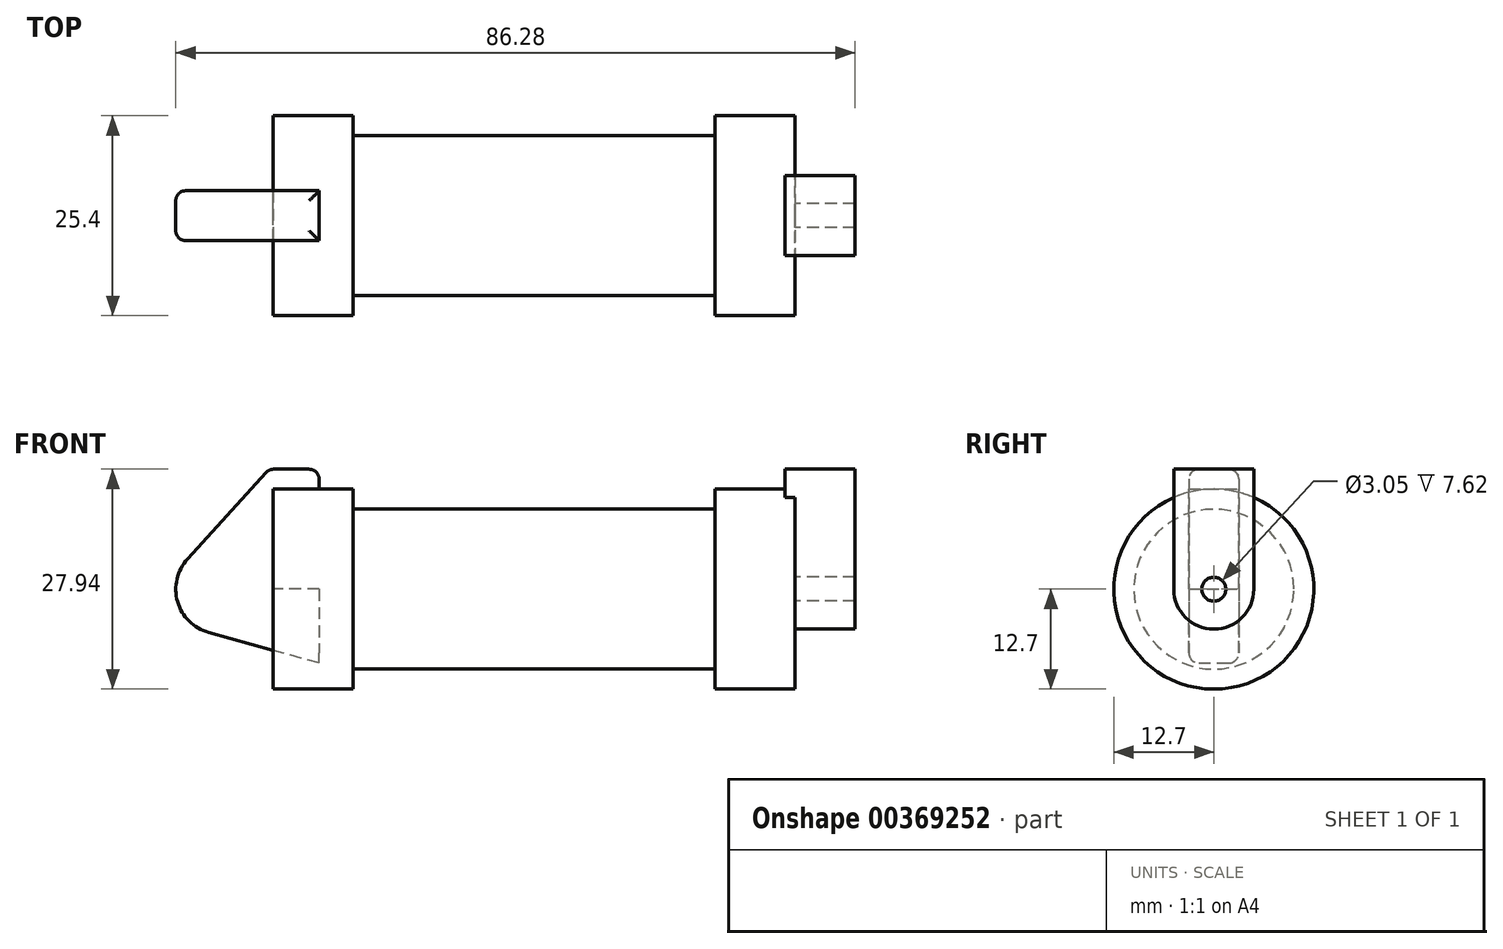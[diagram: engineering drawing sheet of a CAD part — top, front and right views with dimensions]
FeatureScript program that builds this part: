
annotation { "Feature Type Name" : "Feature", "Feature Type Description" : "" }
export const myFeature = defineFeature(function(context is Context, id is Id, definition is map)
    precondition{}
    {
        {
            var Q0;
            Q0=qCreatedBy(makeId("Front.planeOp"),FACE);
            var sketch = newSketch(context, id + "F0", { "sketchPlane" : qUnion([Q0])});
            skLineSegment(sketch, "E0", {"start": v(0, 0) * mm, "end": v(0, 12.7) * mm});
            skLineSegment(sketch, "E1", {"start": v(0, 12.7) * mm, "end": v(10.16, 12.7) * mm});
            skLineSegment(sketch, "E2", {"start": v(10.16, 12.7) * mm, "end": v(10.16, 10.16) * mm});
            skLineSegment(sketch, "E3", {"start": v(10.16, 10.16) * mm, "end": v(56.13, 10.16) * mm});
            skLineSegment(sketch, "E4", {"start": v(56.13, 10.16) * mm, "end": v(56.13, 12.7) * mm});
            skLineSegment(sketch, "E5", {"start": v(56.13, 12.7) * mm, "end": v(66.3, 12.7) * mm});
            skLineSegment(sketch, "E6", {"start": v(66.3, 12.7) * mm, "end": v(66.3, 0) * mm});
            skLineSegment(sketch, "E7", {"start": v(66.3, 0) * mm, "end": v(0, 0) * mm});
            skLineSegment(sketch, "E8", {"start": v(5.84, 15.24) * mm, "end": v(-0.5, 15.24) * mm});
            skLineSegment(sketch, "E9", {"start": v(-0.5, 15.24) * mm, "end": v(-10.88, 3.85) * mm});
            skLineSegment(sketch, "E10", {"start": v(0, 0) * mm, "end": v(-6.65, 0) * mm});
            skCircle(sketch, "E11", {"center": v(-6.65, 0) * mm, "radius": 5.72 * mm});
            skCircle(sketch, "E12", {"center": v(-6.65, 0) * mm, "radius": 3.18 * mm});
            skLineSegment(sketch, "E13", {"start": v(5.84, 15.24) * mm, "end": v(5.84, -9.4) * mm});
            skLineSegment(sketch, "E14", {"start": v(5.84, -9.4) * mm, "end": v(-8.18, -5.5) * mm});
            skSolve(sketch);
        }
        {
            var Q0;
            {var subQ0=sQuery(id+"F0.wireOp",EDGE,"E0");Q0=makeQuery(id+"F0.imprint","IMPRINT",FACE,{"disambiguationData":[TD([[makeQuery(id+"F0.imprint","IMPRINT",EDGE,{"derivedFrom":subQ0}),-1.0]])]});}
            var Q1;
            {var subQ0=sQuery(id+"F0.wireOp",EDGE,"E2");Q1=makeQuery(id+"F0.imprint","IMPRINT",FACE,{"disambiguationData":[TD([[makeQuery(id+"F0.imprint","IMPRINT",EDGE,{"derivedFrom":subQ0}),-1.0]])]});}
            var Q2;
            Q2=sQuery(id+"F0.wireOp",EDGE,"E7");
            revolve(context, id + "F1", {"entities" : qUnion([Q0, Q1]), "axis" : qUnion([Q2]), "revolveType" : RevolveType.FULL});
        }
        {
            var Q0;
            {var subQ1=sQuery(id+"F0.wireOp",EDGE,"E0");Q0=makeQuery(id+"F0.imprint","IMPRINT",FACE,{"disambiguationData":[TD([[makeQuery(id+"F0.imprint","IMPRINT",EDGE,{"derivedFrom":subQ1}),1.0]])]});}
            var Q1;
            {var subQ0=sQuery(id+"F0.wireOp",EDGE,"E14");Q1=makeQuery(id+"F0.imprint","IMPRINT",FACE,{"disambiguationData":[TD([[makeQuery(id+"F0.imprint","IMPRINT",EDGE,{"derivedFrom":subQ0}),-1.0]])]});}
            var Q2;
            {var subQ0=sQuery(id+"F0.wireOp",EDGE,"E12");Q2=makeQuery(id+"F0.imprint","IMPRINT",FACE,{"disambiguationData":[TD([[makeQuery(id+"F0.imprint","IMPRINT",EDGE,{"derivedFrom":subQ0}),1.0]])]});}
            var Q3;
            {var subQ5=sQuery(id+"F0.wireOp",EDGE,"E12");Q3=makeQuery(id+"F0.imprint","IMPRINT",FACE,{"disambiguationData":[TD([[makeQuery(id+"F0.imprint","IMPRINT",EDGE,{"derivedFrom":subQ5}),-1.0]])]});}
            extrude(context, id + "F2", {"entities" : qUnion([Q0, Q1, Q2, Q3]), "endBound" : BoundingType.SYMMETRIC, "depth" : 6.35 * mm});
        }
        {
            var Q0;
            Q0=makeQuery(id+"F1.opRevolve","SWEPT_FACE",FACE,{"disambiguationData":[OSD([sQuery(id+"F0.wireOp",EDGE,"E6")])]});
            var sketch = newSketch(context, id + "F3", { "sketchPlane" : qUnion([Q0])});
            skCircle(sketch, "E15", {"center": v(0, 0) * mm, "radius": 1.52 * mm});
            skCircle(sketch, "E16", {"center": v(0, 0) * mm, "radius": 5.08 * mm});
            skLineSegment(sketch, "E17", {"start": v(5.08, 0) * mm, "end": v(5.08, 15.24) * mm});
            skLineSegment(sketch, "E18", {"start": v(5.08, 15.24) * mm, "end": v(5.08, 0) * mm});
            skLineSegment(sketch, "E19", {"start": v(-5.08, 0) * mm, "end": v(-5.08, 15.24) * mm});
            skLineSegment(sketch, "E20", {"start": v(-5.08, 15.24) * mm, "end": v(5.08, 15.24) * mm});
            skSolve(sketch);
        }
        {
            var Q0;
            Q0 = qSketchRegion(id + "F3", true);
            extrude(context, id + "F4", {"entities" : qUnion([Q0]), "operationType" : NewBodyOperationType.ADD, "depth" : 7.62 * mm, "hasSecondDirection" : true, "secondDirectionOppositeDirection" : true, "secondDirectionDepth" : 1.27 * mm});
        }
        {
            var Q0;
            Q0=makeQuery(id+"F4.opExtrude","SWEPT_FACE",FACE,{"disambiguationData":[OSD([sQuery(id+"F3.wireOp",EDGE,"E20")])]});
            var sketch = newSketch(context, id + "F5", { "sketchPlane" : qUnion([Q0])});
            skCircle(sketch, "E21", {"center": v(69.62, 0) * mm, "radius": 1.52 * mm});
            skSolve(sketch);
        }
        {
            var Q0;
            Q0=sQuery(id+"F5.wireOp",EDGE,"E21");
            extrude(context, id + "F6", {"bodyType" : ToolBodyType.SURFACE, "surfaceEntities" : qUnion([Q0]), "oppositeDirection" : true, "depth" : 10.4 * mm});
        }
        {
            var Q0;
            Q0=makeQuery(id+"F2.opExtrude","SWEPT_FACE",FACE,{"disambiguationData":[OSD([sQuery(id+"F0.wireOp",EDGE,"E8")])]});
            var sketch = newSketch(context, id + "F7", { "sketchPlane" : qUnion([Q0])});
            skCircle(sketch, "E22", {"center": v(2.64, 0) * mm, "radius": 1.55 * mm});
            skPoint(sketch, "E22.centerSnap0", {"position": v(5.84, 0) * mm});
            skSolve(sketch);
        }
        {
            var Q0;
            Q0=sQuery(id+"F7.wireOp",EDGE,"E22");
            extrude(context, id + "F8", {"bodyType" : ToolBodyType.SURFACE, "surfaceEntities" : qUnion([Q0]), "oppositeDirection" : true, "depth" : 17.78 * mm});
        }
        {
            var Q0;
            Q0=makeQuery(id+"F4.opExtrude","SWEPT_EDGE",EDGE,{"disambiguationData":[OSD([sQuery(id+"F3.wireOp",EDGE,"E18"),sQuery(id+"F3.wireOp",EDGE,"E20")])]});
            var Q1;
            Q1=makeQuery(id+"F4.opExtrude","CAP_EDGE",EDGE,{"disambiguationData":[OSD([sQuery(id+"F3.wireOp",EDGE,"E20")])],"isStart":false});
            var Q2;
            Q2=makeQuery(id+"F4.opExtrude","CAP_EDGE",EDGE,{"disambiguationData":[OSD([sQuery(id+"F3.wireOp",EDGE,"E18")])],"isStart":false});
            var Q3;
            Q3=makeQuery(id+"F4.opExtrude","CAP_EDGE",EDGE,{"disambiguationData":[OSD([sQuery(id+"F3.wireOp",EDGE,"E16")])],"isStart":false});
            var Q4;
            Q4=makeQuery(id+"F1.opRevolve","SWEPT_EDGE",EDGE,{"disambiguationData":[OSD([sQuery(id+"F0.wireOp",EDGE,"E5"),sQuery(id+"F0.wireOp",EDGE,"E6")])]});
            var Q5;
            Q5=makeQuery(id+"F1.opRevolve","SWEPT_EDGE",EDGE,{"disambiguationData":[OSD([sQuery(id+"F0.wireOp",EDGE,"E4"),sQuery(id+"F0.wireOp",EDGE,"E5")])]});
            var Q6;
            Q6=makeQuery(id+"F1.opRevolve","SWEPT_EDGE",EDGE,{"disambiguationData":[OSD([sQuery(id+"F0.wireOp",EDGE,"E1"),sQuery(id+"F0.wireOp",EDGE,"E2")])]});
            var Q7;
            Q7=makeQuery(id+"F1.opRevolve","SWEPT_EDGE",EDGE,{"disambiguationData":[OSD([sQuery(id+"F0.wireOp",EDGE,"E2"),sQuery(id+"F0.wireOp",EDGE,"E3")])]});
            var Q8;
            Q8=makeQuery(id+"F1.opRevolve","SWEPT_EDGE",EDGE,{"disambiguationData":[OSD([sQuery(id+"F0.wireOp",EDGE,"E0"),sQuery(id+"F0.wireOp",EDGE,"E1")])]});
            var Q9;
            Q9=makeQuery(id+"F2.opExtrude","CAP_EDGE",EDGE,{"disambiguationData":[OSD([sQuery(id+"F0.wireOp",EDGE,"E8")])],"isStart":true});
            var Q10;
            Q10=makeQuery(id+"F2.opExtrude","SWEPT_EDGE",EDGE,{"disambiguationData":[OSD([sQuery(id+"F0.wireOp",EDGE,"E8"),sQuery(id+"F0.wireOp",EDGE,"E9")])]});
            var Q11;
            Q11=makeQuery(id+"F2.opExtrude","CAP_EDGE",EDGE,{"disambiguationData":[OSD([sQuery(id+"F0.wireOp",EDGE,"E8")])],"isStart":false});
            var Q12;
            Q12=makeQuery(id+"F2.opExtrude","SWEPT_EDGE",EDGE,{"disambiguationData":[OSD([sQuery(id+"F0.wireOp",EDGE,"E8"),sQuery(id+"F0.wireOp",EDGE,"E13")])]});
            var Q13;
            Q13=makeQuery(id+"F2.opExtrude","CAP_EDGE",EDGE,{"disambiguationData":[OSD([sQuery(id+"F0.wireOp",EDGE,"E9")])],"isStart":false});
            var Q14;
            Q14=makeQuery(id+"F2.opExtrude","CAP_EDGE",EDGE,{"disambiguationData":[OSD([sQuery(id+"F0.wireOp",EDGE,"E9")])],"isStart":true});
            var Q15;
            Q15=makeQuery(id+"F2.opExtrude","CAP_EDGE",EDGE,{"disambiguationData":[OSD([sQuery(id+"F0.wireOp",EDGE,"E11")])],"isStart":true});
            var Q16;
            Q16=makeQuery(id+"F2.opExtrude","CAP_EDGE",EDGE,{"disambiguationData":[OSD([sQuery(id+"F0.wireOp",EDGE,"E11")])],"isStart":false});
            var Q17;
            Q17=makeQuery(id+"F2.opExtrude","CAP_EDGE",EDGE,{"disambiguationData":[OSD([sQuery(id+"F0.wireOp",EDGE,"E14")])],"isStart":true});
            var Q18;
            Q18=makeQuery(id+"F4.opExtrude","SWEPT_FACE",FACE,{"disambiguationData":[OSD([sQuery(id+"F3.wireOp",EDGE,"E16")])]});
            var Q19;
            Q19=makeQuery(id+"F4.boolean.opBoolean","INTERSECT",EDGE,{"derivedFrom":[makeQuery(id+"F1.opRevolve","SWEPT_FACE",FACE,{"disambiguationData":[OSD([sQuery(id+"F0.wireOp",EDGE,"E6")])]}),makeQuery(id+"F4.opExtrude","SWEPT_FACE",FACE,{"disambiguationData":[OSD([sQuery(id+"F3.wireOp",EDGE,"E18")])]})]});
            fillet(context, id + "F9", {"entities" : qUnion([Q0, Q1, Q2, Q3, Q4, Q5, Q6, Q7, Q8, Q9, Q10, Q11, Q12, Q13, Q14, Q15, Q16, Q17, Q18, Q19]), "radius" : 1.27 * mm, "tangentPropagation" : true, "allowEdgeOverflow" : false});
        }
    });
